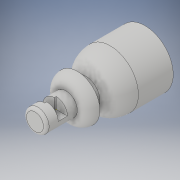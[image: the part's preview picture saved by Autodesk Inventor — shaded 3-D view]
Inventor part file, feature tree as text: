
AUTODESK INVENTOR PART (.ipt)
format: ipt  version: 2018 (Build 220112000, 112)  size: 220,672 bytes
history: native  units: mm
features: sketch x16, extrude x11, fillet x3
ambient origin geometry x8: Origin, YZ Plane, XZ Plane, XY Plane, X Axis, Y Axis, Z Axis, Center Point
bodies: Volumenkörper1 (feature_tree), Volumenkörper2 (feature_tree)
feature tree (30):
  extrude  "Extrusion1"  Depth=2.0mm TaperAngle=0.0deg
  fillet  "Rundung1"  Radius=2.0mm
  extrude  "Extrusion2"  Depth=1.5mm TaperAngle=0.0deg
  extrude  "Extrusion3"  Depth=10.0mm TaperAngle=0.0deg
  extrude  "Extrusion5"  Depth=2.5mm TaperAngle=0.0deg
  extrude  "Extrusion6"  Depth=2.5mm TaperAngle=0.0deg
  extrude  "Extrusion7"  Depth=1.6mm TaperAngle=0.0deg
  fillet  "Rundung2"  Radius=5.0mm
  extrude  "Extrusion9"  Depth=1.75mm TaperAngle=0.0deg
  extrude  "Extrusion12"  Depth=2.0mm TaperAngle=0.0deg
  extrude  "Extrusion13"  Depth=1.75mm TaperAngle=0.0deg
  sketch  "Skizze19"  dims[d51=4.0mm d52=0.35mm d53=0.0mm]
  sketch  "Skizze20"  dims[d55=4.0mm d56=0.35mm d57=0.0mm d58=0.5mm]
  sketch  "Skizze21"
  sketch  "Skizze22"
  sketch  "Skizze24"
  extrude  "Extrusion15"  Depth=0.35mm TaperAngle=0.0deg
  extrude  "Extrusion16"  Depth=0.35mm TaperAngle=0.0deg
  fillet  "Rundung4"  Radius=0.5mm
  sketch  "Skizze1"  dims[d0=8.0mm d1=2.0mm d2=0.0mm d3=2.0mm]
  sketch  "Skizze2"  dims[d4=5.0mm d5=1.5mm d6=0.0mm]
  sketch  "Skizze3"  dims[d7=10.0mm d8=8.0mm d9=0.0mm]
  sketch  "Skizze5"  dims[d13=10.0mm d14=2.5mm d15=0.0mm]
  sketch  "Skizze6"  dims[d16=8.5mm d17=2.5mm d18=0.0mm]
  sketch  "Skizze8"  dims[d19=1.6mm d20=1.6mm d21=0.0mm d22=5.0mm]
  sketch  "Skizze13"  dims[d26=4.0mm d27=1.75mm d28=0.0mm]
  sketch  "Skizze16"  dims[d35=4.0mm d36=2.0mm d37=0.0mm]
  sketch  "Skizze17"  dims[d38=4.0mm d39=1.75mm d40=0.0mm]
  sketch  "Skizze28"
  sketch  "Skizze32"
